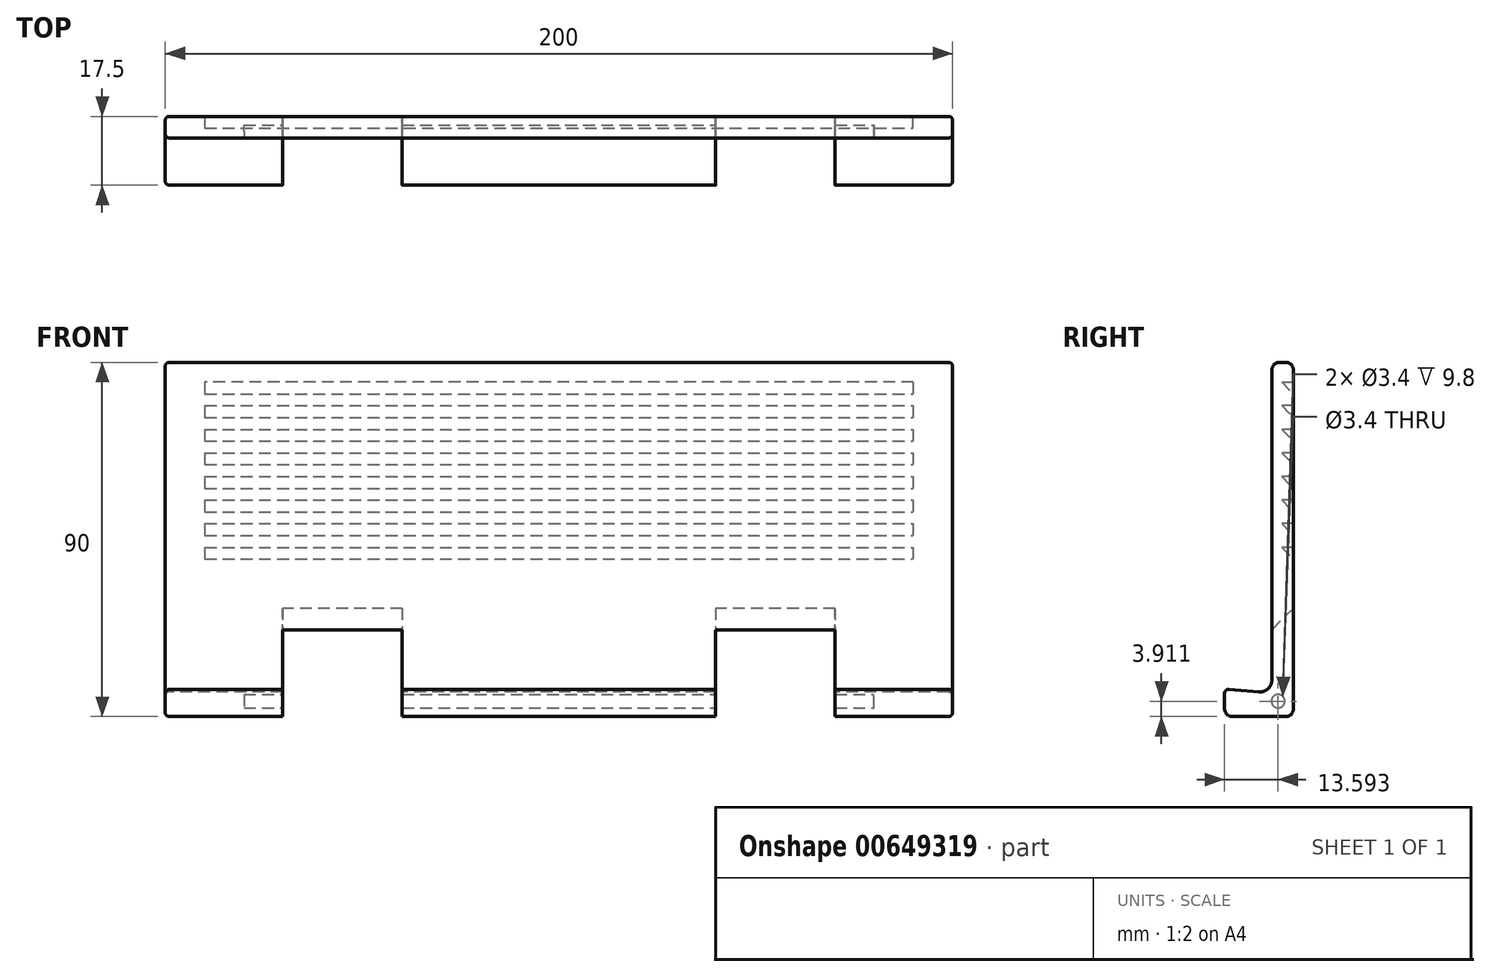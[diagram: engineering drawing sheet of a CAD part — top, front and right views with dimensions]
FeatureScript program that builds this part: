
annotation { "Feature Type Name" : "Feature", "Feature Type Description" : "" }
export const myFeature = defineFeature(function(context is Context, id is Id, definition is map)
    precondition{}
    {
        {
            var Q0;
            Q0=qCreatedBy(makeId("Right.planeOp"),FACE);
            var sketch = newSketch(context, id + "F0", { "sketchPlane" : qUnion([Q0])});
            skLineSegment(sketch, "E0", {"start": v(0, 88) * mm, "end": v(0, 2) * mm});
            skLineSegment(sketch, "E1", {"start": v(-2, 0) * mm, "end": v(-15.5, 0) * mm});
            skLineSegment(sketch, "E2", {"start": v(-5.5, 43.95) * mm, "end": v(-5.5, 88) * mm});
            skLineSegment(sketch, "E3", {"start": v(-3.5, 90) * mm, "end": v(-2, 90) * mm});
            skPoint(sketch, "E4.visualSharp", {"position": v(-5.5, 6) * mm});
            skPoint(sketch, "E5.visualSharp", {"position": v(-17.5, 7) * mm});
            skPoint(sketch, "E6.visualSharp", {"position": v(-17.5, 0) * mm});
            skArc(sketch, "E6.filletArc", {"start": v(-17.5, 2) * mm, "mid": v(-16.91, 0.59) * mm, "end": v(-15.5, 0) * mm});
            skPoint(sketch, "E7.visualSharp", {"position": v(0, 0) * mm});
            skArc(sketch, "E7.filletArc", {"start": v(-2, 0) * mm, "mid": v(-0.59, 0.59) * mm, "end": v(0, 2) * mm});
            skPoint(sketch, "E8.visualSharp", {"position": v(0, 90) * mm});
            skArc(sketch, "E8.filletArc", {"start": v(0, 88) * mm, "mid": v(-0.59, 89.41) * mm, "end": v(-2, 90) * mm});
            skPoint(sketch, "E9.visualSharp", {"position": v(-5.5, 90) * mm});
            skArc(sketch, "E9.filletArc", {"start": v(-3.5, 90) * mm, "mid": v(-4.91, 89.41) * mm, "end": v(-5.5, 88) * mm});
            skLineSegment(sketch, "E10", {"start": v(-9.83, 6.36) * mm, "end": v(-16.42, 6.9) * mm});
            skLineSegment(sketch, "E11", {"start": v(-17.5, 2) * mm, "end": v(-17.5, 5.91) * mm});
            skArc(sketch, "E12.filletArc", {"start": v(-16.42, 6.9) * mm, "mid": v(-17.18, 6.65) * mm, "end": v(-17.5, 5.91) * mm});
            skLineSegment(sketch, "E13", {"start": v(-5.5, 43.95) * mm, "end": v(-5.5, 9.26) * mm});
            skLineSegment(sketch, "E14", {"start": v(-9.83, 6.36) * mm, "end": v(-8.75, 6.27) * mm});
            skArc(sketch, "E15.filletArc", {"start": v(-8.75, 6.27) * mm, "mid": v(-6.47, 7.05) * mm, "end": v(-5.5, 9.26) * mm});
            skSolve(sketch);
        }
        {
            var Q0;
            Q0=makeQuery(id+"F0.imprint","IMPRINT",FACE,{"disambiguationData":[TD([[makeQuery(id+"F0.imprint","IMPRINT",EDGE,{"derivedFrom":sQuery(id+"F0.wireOp",EDGE,"E0")}),-1.0]])]});
            extrude(context, id + "F1", {"entities" : qUnion([Q0]), "depth" : 100 * mm, "offsetDistance" : 25 * mm, "hasSecondDirection" : true, "secondDirectionOppositeDirection" : true, "secondDirectionDepth" : 100 * mm});
        }
        {
            var Q0;
            Q0=makeQuery(id+"F1.opExtrude","CAP_EDGE",EDGE,{"disambiguationData":[OSD([sQuery(id+"F0.wireOp",EDGE,"E0")])],"isStart":true});
            var Q1;
            Q1=makeQuery(id+"F1.opExtrude","CAP_EDGE",EDGE,{"disambiguationData":[OSD([sQuery(id+"F0.wireOp",EDGE,"E0")])],"isStart":false});
            fillet(context, id + "F2", {"entities" : qUnion([Q0, Q1]), "radius" : 1 * mm, "tangentPropagation" : true, "allowEdgeOverflow" : false});
        }
        {
            var Q0;
            Q0=makeQuery(id+"F1.opExtrude","CAP_FACE",FACE,{"disambiguationData":[OSD([sQuery(id+"F0.wireOp",EDGE,"E0"),sQuery(id+"F0.wireOp",EDGE,"E1"),sQuery(id+"F0.wireOp",EDGE,"E2"),sQuery(id+"F0.wireOp",EDGE,"E3"),sQuery(id+"F0.wireOp",EDGE,"E6.filletArc"),sQuery(id+"F0.wireOp",EDGE,"E7.filletArc"),sQuery(id+"F0.wireOp",EDGE,"E8.filletArc"),sQuery(id+"F0.wireOp",EDGE,"E9.filletArc"),sQuery(id+"F0.wireOp",EDGE,"E10"),sQuery(id+"F0.wireOp",EDGE,"E11"),sQuery(id+"F0.wireOp",EDGE,"E12.filletArc"),sQuery(id+"F0.wireOp",EDGE,"E13"),sQuery(id+"F0.wireOp",EDGE,"E14"),sQuery(id+"F0.wireOp",EDGE,"E15.filletArc")])],"isStart":false});
            var sketch = newSketch(context, id + "F3", { "sketchPlane" : qUnion([Q0])});
            skCircle(sketch, "E16", {"center": v(-3.9, 3.91) * mm, "radius": 1.7 * mm});
            skSolve(sketch);
        }
        {
            var Q0;
            Q0=qCreatedBy(makeId("Right.planeOp"),FACE);
            var sketch = newSketch(context, id + "F4", { "sketchPlane" : qUnion([Q0])});
            skLineSegment(sketch, "E17", {"start": v(-19.34, 7.67) * mm, "end": v(-19.34, 0) * mm});
            skLineSegment(sketch, "E18", {"start": v(-19.34, 0) * mm, "end": v(0, 0) * mm});
            skLineSegment(sketch, "E19", {"start": v(0, 0) * mm, "end": v(0, 27.5) * mm});
            skLineSegment(sketch, "E20", {"start": v(0, 27.5) * mm, "end": v(-5.5, 22) * mm});
            skLineSegment(sketch, "E21", {"start": v(-5.5, 22) * mm, "end": v(-5.5, 9.47) * mm});
            skLineSegment(sketch, "E22", {"start": v(-5.5, 9.47) * mm, "end": v(-8.88, 6.7) * mm});
            skLineSegment(sketch, "E23", {"start": v(-8.88, 6.7) * mm, "end": v(-19.34, 7.67) * mm});
            skSolve(sketch);
        }
        {
            var Q0;
            Q0 = qSketchRegion(id + "F4", true);
            extrude(context, id + "F5", {"entities" : qUnion([Q0]), "operationType" : NewBodyOperationType.REMOVE, "depth" : 70.2 * mm, "offsetDistance" : 25 * mm, "hasSecondDirection" : true, "secondDirectionOppositeDirection" : true, "secondDirectionDepth" : 70.2 * mm});
        }
        {
            var Q0;
            Q0 = qSketchRegion(id + "F0", true);
            extrude(context, id + "F6", {"entities" : qUnion([Q0]), "operationType" : NewBodyOperationType.ADD, "depth" : 39.8 * mm, "offsetDistance" : 25 * mm, "hasSecondDirection" : true, "secondDirectionOppositeDirection" : true, "secondDirectionDepth" : 39.8 * mm});
        }
        {
            var Q0;
            Q0 = qSketchRegion(id + "F3", true);
            extrude(context, id + "F7", {"entities" : qUnion([Q0]), "operationType" : NewBodyOperationType.REMOVE, "endBound" : BoundingType.THROUGH_ALL, "oppositeDirection" : true, "depth" : 25 * mm, "offsetDistance" : 25 * mm});
        }
        {
            var Q0;
            Q0=qCreatedBy(makeId("Right.planeOp"),FACE);
            var sketch = newSketch(context, id + "F8", { "sketchPlane" : qUnion([Q0])});
            skLineSegment(sketch, "E24", {"start": v(0, 85) * mm, "end": v(-3, 85) * mm});
            skLineSegment(sketch, "E25", {"start": v(-3, 85) * mm, "end": v(0, 82) * mm});
            skLineSegment(sketch, "E26", {"start": v(0, 82) * mm, "end": v(0, 79) * mm});
            skLineSegment(sketch, "E27", {"start": v(0, 79) * mm, "end": v(-3, 79) * mm});
            skLineSegment(sketch, "E28", {"start": v(-3, 79) * mm, "end": v(0, 76) * mm});
            skLineSegment(sketch, "E29", {"start": v(0, 76) * mm, "end": v(0, 73) * mm});
            skLineSegment(sketch, "E30", {"start": v(0, 73) * mm, "end": v(-3, 73) * mm});
            skLineSegment(sketch, "E31", {"start": v(-3, 73) * mm, "end": v(0, 70) * mm});
            skLineSegment(sketch, "E32", {"start": v(0, 70) * mm, "end": v(0, 67) * mm});
            skLineSegment(sketch, "E33", {"start": v(0, 67) * mm, "end": v(-3, 67) * mm});
            skLineSegment(sketch, "E34", {"start": v(-3, 67) * mm, "end": v(0, 64) * mm});
            skLineSegment(sketch, "E35", {"start": v(0, 64) * mm, "end": v(0, 61) * mm});
            skLineSegment(sketch, "E36", {"start": v(0, 61) * mm, "end": v(-3, 61) * mm});
            skLineSegment(sketch, "E37", {"start": v(-3, 61) * mm, "end": v(0, 58) * mm});
            skLineSegment(sketch, "E38", {"start": v(0, 58) * mm, "end": v(0, 55) * mm});
            skLineSegment(sketch, "E39", {"start": v(0, 55) * mm, "end": v(-3, 55) * mm});
            skLineSegment(sketch, "E40", {"start": v(-3, 55) * mm, "end": v(0, 52) * mm});
            skLineSegment(sketch, "E41", {"start": v(0, 52) * mm, "end": v(0, 49) * mm});
            skLineSegment(sketch, "E42", {"start": v(0, 49) * mm, "end": v(-3, 49) * mm});
            skLineSegment(sketch, "E43", {"start": v(-3, 49) * mm, "end": v(0, 46) * mm});
            skLineSegment(sketch, "E44", {"start": v(0, 46) * mm, "end": v(0, 43) * mm});
            skLineSegment(sketch, "E45", {"start": v(0, 43) * mm, "end": v(-3, 43) * mm});
            skLineSegment(sketch, "E46", {"start": v(-3, 43) * mm, "end": v(0, 40) * mm});
            skLineSegment(sketch, "E47", {"start": v(0, 85) * mm, "end": v(1.85, 85) * mm});
            skLineSegment(sketch, "E48", {"start": v(1.85, 85) * mm, "end": v(1.85, 39.9) * mm});
            skLineSegment(sketch, "E49", {"start": v(1.85, 39.9) * mm, "end": v(0, 40) * mm});
            skSolve(sketch);
        }
        {
            var Q0;
            Q0 = qSketchRegion(id + "F8", true);
            extrude(context, id + "F9", {"entities" : qUnion([Q0]), "operationType" : NewBodyOperationType.REMOVE, "oppositeDirection" : true, "depth" : 90 * mm, "offsetDistance" : 25 * mm, "hasSecondDirection" : true, "secondDirectionOppositeDirection" : false, "secondDirectionDepth" : 90 * mm});
        }
        {
            var Q0;
            Q0=makeQuery(id+"F1.opExtrude","CAP_FACE",FACE,{"disambiguationData":[OSD([sQuery(id+"F0.wireOp",EDGE,"E0"),sQuery(id+"F0.wireOp",EDGE,"E1"),sQuery(id+"F0.wireOp",EDGE,"E2"),sQuery(id+"F0.wireOp",EDGE,"E3"),sQuery(id+"F0.wireOp",EDGE,"E6.filletArc"),sQuery(id+"F0.wireOp",EDGE,"E7.filletArc"),sQuery(id+"F0.wireOp",EDGE,"E8.filletArc"),sQuery(id+"F0.wireOp",EDGE,"E9.filletArc"),sQuery(id+"F0.wireOp",EDGE,"E10"),sQuery(id+"F0.wireOp",EDGE,"E11"),sQuery(id+"F0.wireOp",EDGE,"E12.filletArc"),sQuery(id+"F0.wireOp",EDGE,"E13"),sQuery(id+"F0.wireOp",EDGE,"E14"),sQuery(id+"F0.wireOp",EDGE,"E15.filletArc")])],"isStart":false});
            var sketch = newSketch(context, id + "F10", { "sketchPlane" : qUnion([Q0])});
            skCircle(sketch, "E50", {"center": v(-3.9, 3.91) * mm, "radius": 1.7 * mm});
            skSolve(sketch);
        }
        {
            var Q0;
            Q0 = qSketchRegion(id + "F10", true);
            extrude(context, id + "F11", {"entities" : qUnion([Q0]), "operationType" : NewBodyOperationType.ADD, "oppositeDirection" : true, "depth" : 20 * mm, "offsetDistance" : 25 * mm});
        }
        {
            var Q0;
            Q0=makeQuery(id+"F1.opExtrude","CAP_FACE",FACE,{"disambiguationData":[OSD([sQuery(id+"F0.wireOp",EDGE,"E0"),sQuery(id+"F0.wireOp",EDGE,"E1"),sQuery(id+"F0.wireOp",EDGE,"E2"),sQuery(id+"F0.wireOp",EDGE,"E3"),sQuery(id+"F0.wireOp",EDGE,"E6.filletArc"),sQuery(id+"F0.wireOp",EDGE,"E7.filletArc"),sQuery(id+"F0.wireOp",EDGE,"E8.filletArc"),sQuery(id+"F0.wireOp",EDGE,"E9.filletArc"),sQuery(id+"F0.wireOp",EDGE,"E10"),sQuery(id+"F0.wireOp",EDGE,"E11"),sQuery(id+"F0.wireOp",EDGE,"E12.filletArc"),sQuery(id+"F0.wireOp",EDGE,"E13"),sQuery(id+"F0.wireOp",EDGE,"E14"),sQuery(id+"F0.wireOp",EDGE,"E15.filletArc")])],"isStart":true});
            var sketch = newSketch(context, id + "F12", { "sketchPlane" : qUnion([Q0])});
            skCircle(sketch, "E51", {"center": v(3.9, 3.91) * mm, "radius": 2.17 * mm});
            skSolve(sketch);
        }
        {
            var Q0;
            Q0 = qSketchRegion(id + "F12", true);
            extrude(context, id + "F13", {"entities" : qUnion([Q0]), "operationType" : NewBodyOperationType.ADD, "oppositeDirection" : true, "depth" : 20 * mm, "offsetDistance" : 25 * mm});
        }
    });
